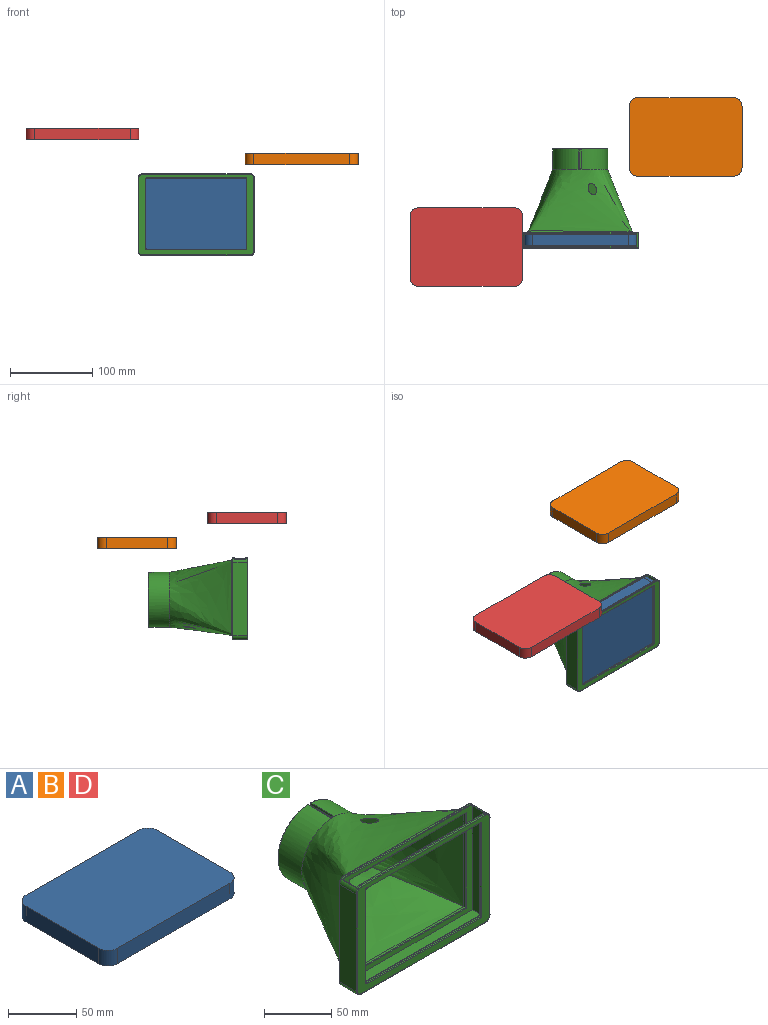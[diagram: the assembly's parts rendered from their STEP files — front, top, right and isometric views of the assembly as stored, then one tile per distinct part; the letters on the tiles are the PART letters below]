
ASSEMBLY  parts=4 mates=1
PART A: 10 faces, bbox 136.7x95.3x14 mm
  f0: plane 74.93x13.97mm, normal (-1,0,0), area 1046.8mm2, adj f4,f5,f6,f9
  f1: plane 116.33x13.97mm, normal (0,-1,0), area 1625.2mm2, adj f4,f5,f6,f7
  f2: plane 74.93x13.97mm, normal (1,0,0), area 1046.8mm2, adj f4,f5,f7,f8
  f3: plane 116.33x13.97mm, normal (0,1,0), area 1625.2mm2, adj f4,f5,f8,f9
  f4: plane 136.65x95.25mm, normal (0,0,1), area 12927.5mm2, adj f0,f1,f2,f3,f6,f7,f8,f9
  f5: plane 136.65x95.25mm, normal (0,0,-1), area 12927.5mm2, adj f0,f1,f2,f3,f6,f7,f8,f9
  f6: cylinder r=10.16mm len=13.97mm, axis (0,0,-1), area 223mm2, adj f0,f1,f4,f5
  f7: cylinder r=10.16mm len=13.97mm, axis (0,0,1), area 223mm2, adj f1,f2,f4,f5
  f8: cylinder r=10.16mm len=13.97mm, axis (0,0,-1), area 223mm2, adj f2,f3,f4,f5
  f9: cylinder r=10.16mm len=13.97mm, axis (0,0,1), area 223mm2, adj f0,f3,f4,f5
PART B: same geometry as A
PART C: 96 faces, bbox 141.8x120.7x99.9 mm
  f0: cylinder r=30.73mm len=61.47mm, axis (0,-1,0), area 4722.4mm2, adj f27,f28,f29,f30,f69,f72,f73,f74
  f1: cylinder r=33.27mm len=66.55mm, axis (0,-1,0), area 5129.8mm2, adj f26,f34,f63,f64,f65
  f2: plane 130.81x1.27mm, normal (0,0,1), area 166.1mm2, adj f24,f25,f61,f82
  f3: plane 88.9x17.53mm, normal (-1,0,0), area 1558.1mm2, adj f22,f25,f86,f94
  f4: plane 130.81x17.53mm, normal (0,0,-1), area 2292.6mm2, adj f22,f23,f83,f91
  f5: plane 88.9x17.53mm, normal (1,0,0), area 1558.1mm2, adj f23,f24,f79,f87
  f6: plane 130.81x1.27mm, normal (0,0,1), area 166.1mm2, adj f24,f25,f56,f90
  f7: plane 139.45x97.54mm, normal (0,-1,0), area 2846.1mm2, adj f39,f40,f41,f42,f43,f44,f45,f46
  f8: plane 139.45x97.54mm, normal (0,1,0), area 1330.4mm2, adj f87,f88,f89,f90,f91,f92,f93,f94
  f9: plane 94.85x13.97mm, normal (1,0,0), area 1325mm2, adj f10,f12,f13,f60
  f10: plane 136.11x96.01mm, normal (0,1,0), area 2306.9mm2, adj f9,f11,f13,f47,f48,f49,f50,f51
  f11: plane 94.85x13.97mm, normal (-1,0,0), area 1325mm2, adj f10,f12,f13,f57
  f12: plane 136.11x96.01mm, normal (0,-1,0), area 2304.2mm2, adj f9,f11,f13,f55,f56,f57,f58,f60
  f13: plane 135.89x13.97mm, normal (0,0,1), area 1898.4mm2, adj f9,f10,f11,f12
  f14: plane 121.92x2.03mm, normal (0,0,-1), area 247.7mm2, adj f15,f17,f30,f76
  f15: plane 86.36x2.03mm, normal (-1,0,0), area 175.5mm2, adj f14,f16,f29,f75
  f16: plane 121.92x2.03mm, normal (0,0,1), area 247.7mm2, adj f15,f17,f28,f77
  f17: plane 86.36x2.03mm, normal (1,0,0), area 175.5mm2, adj f14,f16,f27,f78
  f18: plane 83.82x1.52mm, normal (1,0,0), area 127.7mm2, adj f35,f37,f40,f49
  f19: plane 119.38x1.52mm, normal (0,0,1), area 181.9mm2, adj f35,f36,f41,f48
  f20: plane 83.82x1.52mm, normal (-1,0,0), area 127.7mm2, adj f36,f38,f45,f52
  f21: plane 119.38x1.52mm, normal (0,0,-1), area 181.9mm2, adj f37,f38,f44,f53
  f22: cylinder r=5.08mm len=17.53mm, axis (0,1,0), area 139.9mm2, adj f3,f4,f85,f93
  f23: cylinder r=5.08mm len=17.53mm, axis (0,-1,0), area 139.9mm2, adj f4,f5,f81,f89
  f24: cylinder r=5.08mm len=17.53mm, axis (0,1,0), area 84.3mm2, adj f2,f5,f6,f55,f57,f59,f80,f88
  f25: cylinder r=5.08mm len=17.53mm, axis (0,-1,0), area 84.3mm2, adj f2,f3,f6,f58,f60,f62,f84,f92
  f26: bspline ~126.26x91.13mm, area 24754.5mm2, adj f1,f28,f30,f95
  f27: bspline ~86.36x76.2mm, area 5531.4mm2, adj f0,f17,f28,f30
  f28: bspline ~121.92x76.2mm, area 6422.2mm2, adj f0,f16,f26,f27,f29
  f29: bspline ~86.36x76.2mm, area 5538.2mm2, adj f0,f15,f28,f30
  f30: bspline ~121.92x76.2mm, area 6515.7mm2, adj f0,f14,f26,f27,f29
  f31: plane 65.53x65.48mm, normal (0,1,0), area 301mm2, adj f65,f67,f68,f69
  f32: plane 2.54x1.55mm, normal (0,1,0), area 3.9mm2, adj f33,f34,f63,f64,f74
  f33: plane 23.62x1.53mm, normal (1,0,0), area 36.1mm2, adj f32,f64,f68,f73,f74
  f34: plane 24.14x2.07mm, normal (-1,0,0), area 48.7mm2, adj f1,f32,f63,f67,f72,f74
  f35: cylinder r=1.27mm len=1.52mm, axis (0,1,0), area 3mm2, adj f18,f19,f39,f47
  f36: cylinder r=1.27mm len=1.52mm, axis (0,-1,0), area 3mm2, adj f19,f20,f43,f50
  f37: cylinder r=1.27mm len=1.52mm, axis (0,-1,0), area 3mm2, adj f18,f21,f42,f51
  f38: cylinder r=1.27mm len=1.52mm, axis (0,1,0), area 3mm2, adj f20,f21,f46,f54
  f39: torus R=1.78mm, axis (0,-1,0), area 1.8mm2, adj f7,f35,f40,f41
  f40: cylinder r=0.51mm len=83.82mm, axis (0,0,1), area 66.9mm2, adj f7,f18,f39,f42
  f41: cylinder r=0.51mm len=119.38mm, axis (-1,0,0), area 95.3mm2, adj f7,f19,f39,f43
  f42: torus R=1.78mm, axis (0,-1,0), area 1.8mm2, adj f7,f37,f40,f44
  f43: torus R=1.78mm, axis (0,-1,0), area 1.8mm2, adj f7,f36,f41,f45
  f44: cylinder r=0.51mm len=119.38mm, axis (1,0,0), area 95.3mm2, adj f7,f21,f42,f46
  f45: cylinder r=0.51mm len=83.82mm, axis (0,0,-1), area 66.9mm2, adj f7,f20,f43,f46
  f46: torus R=1.78mm, axis (0,-1,0), area 1.8mm2, adj f7,f38,f44,f45
  f47: torus R=1.78mm, axis (0,-1,0), area 1.8mm2, adj f10,f35,f48,f49
  f48: cylinder r=0.51mm len=119.38mm, axis (1,0,0), area 95.3mm2, adj f10,f19,f47,f50
  f49: cylinder r=0.51mm len=83.82mm, axis (0,0,-1), area 66.9mm2, adj f10,f18,f47,f51
  f50: torus R=1.78mm, axis (0,-1,0), area 1.8mm2, adj f10,f36,f48,f52
  f51: torus R=1.78mm, axis (0,-1,0), area 1.8mm2, adj f10,f37,f49,f53
  f52: cylinder r=0.51mm len=83.82mm, axis (0,0,1), area 66.9mm2, adj f10,f20,f50,f54
  f53: cylinder r=0.51mm len=119.38mm, axis (-1,0,0), area 95.3mm2, adj f10,f21,f51,f54
  f54: torus R=1.78mm, axis (0,-1,0), area 1.8mm2, adj f10,f38,f52,f53
  f55: torus R=4.57mm, axis (0,-1,0), area 2.6mm2, adj f12,f24,f56,f57
  f56: cylinder r=0.51mm len=130.81mm, axis (1,0,0), area 104.4mm2, adj f6,f12,f55,f58
  f57: cylinder r=0.51mm len=14.99mm, axis (0,1,0), area 16.7mm2, adj f10,f11,f12,f24,f55,f59
  f58: torus R=4.57mm, axis (0,-1,0), area 2.6mm2, adj f12,f25,f56,f60
  f59: torus R=4.57mm, axis (0,-1,0), area 2.6mm2, adj f10,f24,f57,f61
  f60: cylinder r=0.51mm len=14.99mm, axis (0,-1,0), area 16.7mm2, adj f9,f10,f12,f25,f58,f62
  f61: cylinder r=0.51mm len=130.81mm, axis (-1,0,0), area 104.4mm2, adj f2,f10,f59,f62
  f62: torus R=4.57mm, axis (0,-1,0), area 2.6mm2, adj f10,f25,f60,f61
  f63: torus R=32.77mm, axis (0,1,0), area 2.2mm2, adj f1,f32,f34,f64
  f64: cylinder r=0.51mm len=24.13mm, axis (0,-1,0), area 19.6mm2, adj f1,f32,f33,f63,f66
  f65: torus R=32.77mm, axis (0,-1,0), area 163.2mm2, adj f1,f31,f66,f67
  f66: sphere r=0.51mm, area 0.4mm2, adj f64,f65,f68
  f67: cylinder r=0.51mm len=2.06mm, axis (0,0,-1), area 1.4mm2, adj f31,f34,f65,f70
  f68: cylinder r=0.51mm len=1.53mm, axis (0,0,1), area 1.2mm2, adj f31,f33,f66,f71
  f69: torus R=31.24mm, axis (0,-1,0), area 152.2mm2, adj f0,f31,f70,f71
  f70: sphere r=0.51mm, area 0.3mm2, adj f67,f69,f72
  f71: sphere r=0.51mm, area 0.3mm2, adj f68,f69,f73
  f72: cylinder r=0.51mm len=24.13mm, axis (0,-1,0), area 18.4mm2, adj f0,f34,f70,f74
  f73: cylinder r=0.51mm len=24.13mm, axis (0,-1,0), area 18.4mm2, adj f0,f33,f71,f74
  f74: torus R=31.24mm, axis (0,1,0), area 2.3mm2, adj f0,f32,f33,f34,f72,f73
  f75: cylinder r=0.51mm len=87.38mm, axis (0,0,-1), area 69.3mm2, adj f12,f15,f76,f77
  f76: cylinder r=0.51mm len=122.94mm, axis (1,0,0), area 97.7mm2, adj f12,f14,f75,f78
  f77: cylinder r=0.51mm len=122.94mm, axis (-1,0,0), area 97.7mm2, adj f12,f16,f75,f78
  f78: cylinder r=0.51mm len=87.38mm, axis (0,0,1), area 69.3mm2, adj f12,f17,f76,f77
  f79: cylinder r=0.76mm len=88.9mm, axis (0,0,-1), area 106.4mm2, adj f5,f7,f80,f81
  f80: torus R=4.32mm, axis (0,-1,0), area 9mm2, adj f7,f24,f79,f82
  f81: torus R=4.32mm, axis (0,-1,0), area 9mm2, adj f7,f23,f79,f83
  f82: cylinder r=0.76mm len=130.81mm, axis (1,0,0), area 156.6mm2, adj f2,f7,f80,f84
  f83: cylinder r=0.76mm len=130.81mm, axis (-1,0,0), area 156.6mm2, adj f4,f7,f81,f85
  f84: torus R=4.32mm, axis (0,-1,0), area 9mm2, adj f7,f25,f82,f86
  f85: torus R=4.32mm, axis (0,-1,0), area 9mm2, adj f7,f22,f83,f86
  f86: cylinder r=0.76mm len=88.9mm, axis (0,0,1), area 106.4mm2, adj f3,f7,f84,f85
  f87: cylinder r=0.76mm len=88.9mm, axis (0,0,1), area 106.4mm2, adj f5,f8,f88,f89
  f88: torus R=4.32mm, axis (0,-1,0), area 9mm2, adj f8,f24,f87,f90
  f89: torus R=4.32mm, axis (0,-1,0), area 9mm2, adj f8,f23,f87,f91
  f90: cylinder r=0.76mm len=130.81mm, axis (-1,0,0), area 156.6mm2, adj f6,f8,f88,f92
  f91: cylinder r=0.76mm len=130.81mm, axis (1,0,0), area 156.6mm2, adj f4,f8,f89,f93
  f92: torus R=4.32mm, axis (0,-1,0), area 9mm2, adj f8,f25,f90,f94
  f93: torus R=4.32mm, axis (0,-1,0), area 9mm2, adj f8,f22,f91,f94
  f94: cylinder r=0.76mm len=88.9mm, axis (0,0,-1), area 106.4mm2, adj f3,f8,f92,f93
  f95: bspline ~129.73x94.86mm, area 1106mm2, adj f8,f26
PART D: same geometry as A
PLACE A rot(axis=(-1,0,0),90deg) t=(0.54,-16.99,2.82)mm
PLACE B t=(127.81,115.08,61.92)mm
PLACE C t=(0,-0.48,0)mm
PLACE D t=(-138.13,-18.49,91.9)mm
MATE planar A.f4 <-> C.f12  axis (0,1,0) through (0.54,-3.02,50.44)mm
